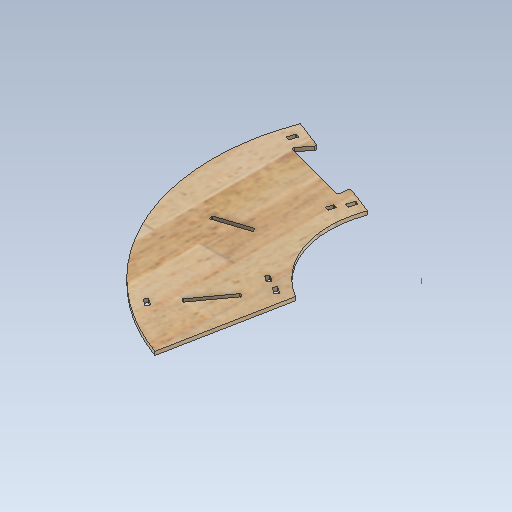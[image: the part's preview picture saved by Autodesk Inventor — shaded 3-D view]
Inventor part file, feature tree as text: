
AUTODESK INVENTOR PART (.ipt)
format: ipt  version: 2020 (Build 240168000, 168)  size: 588,288 bytes
history: native  units: mm
features: extrude x7, sketch x5, pattern_circular x4, mirror x3, plane x1
ambient origin geometry x8: Origin, YZ Plane, XZ Plane, XY Plane, X Axis, Y Axis, Z Axis, Center Point
bodies: Body1 (feature_tree)
feature tree (20):
  extrude  "Extrusion3"  Depth=6.5mm
  extrude  "Extrusion4"  Depth=2.666667mm
  extrude  "Extrusion5"  Depth=1.333333mm
  sketch  "Sketch5"  dims[d25=2.666667mm d32=1.333333mm]
  extrude  "Extrusion7"  TaperAngle=0.0deg  [1 undecoded]
  sketch  "Sketch7"  dims[d40=3.25mm d41=90.0deg d42=3.25mm d43=90.0deg d47=50.0mm d49=360.0deg d52=4.363323mm d54=10.0mm d55=0.0mm d60=0.872665mm d61=12.566371mm d62=13.439035mm d63=2.666667mm d64=0.523599mm d66=0.523599mm d67=2.666667mm d68=2.666667mm d70=12.566371mm d71=12.566371mm d84=300.14mm d85=682.72mm d86=491.43mm d87=150.07mm d88=341.36mm d89=4.363323mm d90=1.919862mm d91=1.919862mm d94=300.14mm d95=682.72mm d96=0.24305mm d104=6.5mm d105=12.0mm d108=1.333333mm d109=1.333333mm d110=1.333333mm d111=1.333333mm d112=0.0mm d113=0.0mm d114=0.0mm d116=1.333333mm d117=1.333333mm d119=1.333333mm d120=1.333333mm d121=6.5mm d122=10.0mm d123=0.0mm d124=0.0mm d126=1.09mm d127=16.333333mm d128=1.333333mm d129=1.333333mm d130=1.333333mm d131=1.333333mm d132=6.5mm d133=10.0mm d135=0.523599mm d137=0.0mm d138=0.0mm d140=0.666667mm d141=3.25mm d142=20.0mm d143=12.566371mm d145=20.0mm d146=12.566371mm d148=0.27mm d149=145.0mm d150=90.0deg d151=90.0deg d152=90.0deg d153=90.0deg d154=20.0mm d155=25.132741mm d157=20.0mm d158=25.132741mm d160=0.0mm d161=0.0mm]
  extrude  "Extrusion8"  TaperAngle=90.0deg  [1 undecoded]
  extrude  "Extrusion9"  Depth=145.0mm
  plane  "Work Plane1"
  mirror  "Mirror2"
  mirror  "Mirror1"
  pattern_circular  "Circular Pattern1"  Angle=90.0deg  [1 undecoded]
  pattern_circular  "Circular Pattern2"  Count=5 Angle=360.0deg
  pattern_circular  "Circular Pattern3"  [2 undecoded]
  mirror  "Mirror3"
  pattern_circular  "Circular Pattern4"  [2 undecoded]
  extrude  "Extrusion10"  Depth=145.0mm
  sketch  "Sketch2"  dims[d15=6.0mm d16=0.0mm d21=6.5mm]
  sketch  "Sketch3"  dims[d23=66.666667mm d24=2.666667mm]
  sketch  "Sketch6"  dims[d33=1.333333mm d38=0.0mm d39=0.0mm]
note: 7 required parameter values undecoded (feature->parameter linkage not recoverable at this tier; creation-order binding heuristic only, values carry confidence <= 0.55)
